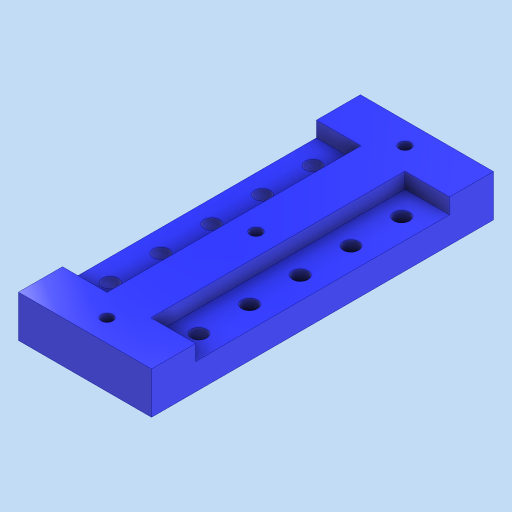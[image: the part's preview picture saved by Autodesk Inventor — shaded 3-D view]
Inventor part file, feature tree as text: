
AUTODESK INVENTOR PART (.ipt)
format: ipt  version: 2023 (Build 270158000, 158)  size: 215,552 bytes
history: native  units: in
note: dims shown in document units (in); Inventor stores cm internally (conversion verified against a paired STEP export)
features: extrude x3, sketch x2, other x1, plane x1, mirror x1, projected_geometry x1
ambient origin geometry x8: Origin, YZ Plane, XZ Plane, XY Plane, X Axis, Y Axis, Z Axis, Center Point
bodies: Solid1 (feature_tree)
feature tree (9):
  parser-record x1  (decoder bookkeeping rows leaked as tree rows — omitted from the tree; the rows remain in map.json)
  sketch  "Sketch1"  dims[d0=4.5354in d1=0.7953in]
  extrude  "Extrusion1"  Depth=0.7953in
  extrude  "Extrusion2"  Depth=0.7874in
  extrude  "Extrusion3"  Depth=0.7874in
  sketch  "Sketch2"  dims[d2=0.2756in d3=0.9055in d4=0.9055in d5=0.4724in d6=0.0in d7=0.0787in d8=0.0in d9=0.748in d10=0.0in d11=0.7874in d12=0.7874in d13=0.7874in d14=0.2047in d15=90.0deg]
  plane  "Work Plane1"
  mirror  "Mirror1"
  projected_geometry  "Projected Loop1"
note: 1 file-system path scrubbed to <path> (originals preserved in map.json)
